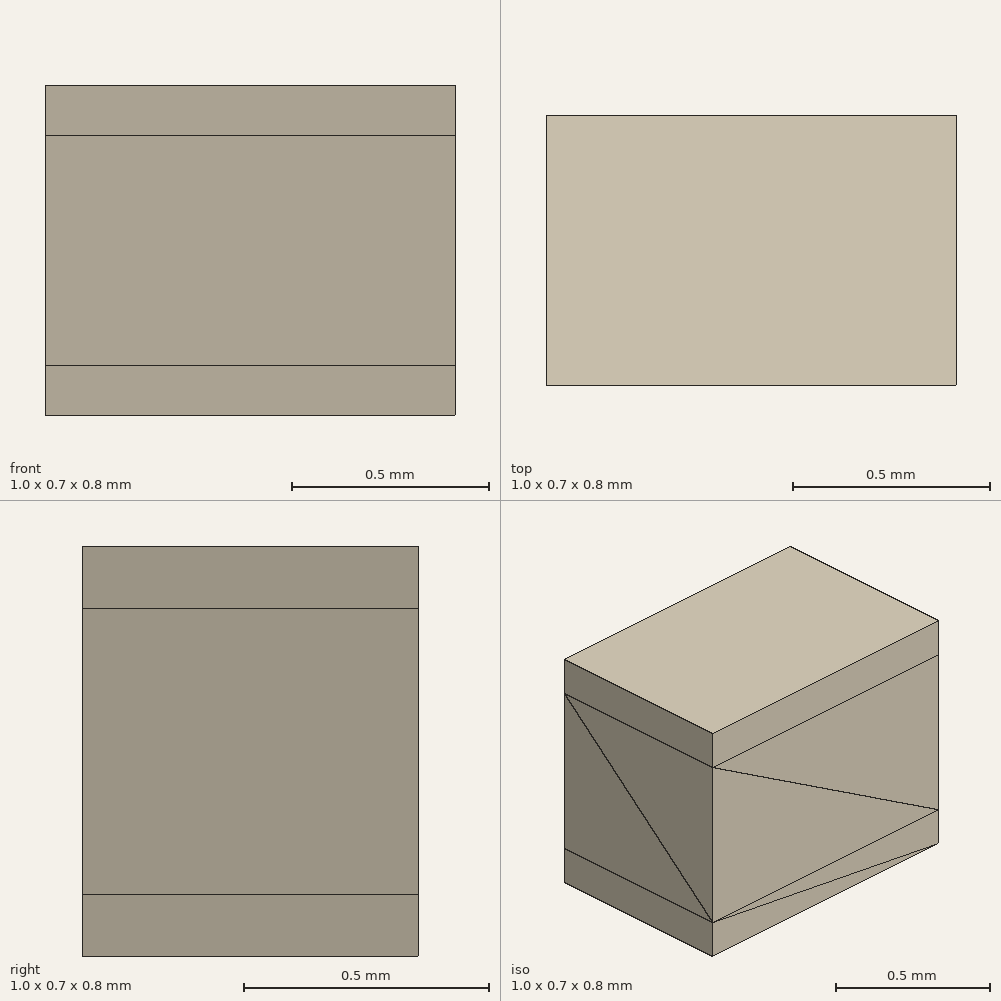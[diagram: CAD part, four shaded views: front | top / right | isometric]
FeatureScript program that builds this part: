
annotation { "Feature Type Name" : "Feature", "Feature Type Description" : "" }
export const myFeature = defineFeature(function(context is Context, id is Id, definition is map)
    precondition{}
    {
        {
            var Q0;
            Q0=qCreatedBy(makeId("Top.planeOp"),FACE);
            var sketch = newSketch(context, id + "F0", { "sketchPlane" : qUnion([Q0])});
            skLineSegment(sketch, "E0.bottom", {"start": v(-0.52, 0.34) * mm, "end": v(0.52, 0.34) * mm});
            skLineSegment(sketch, "E0.top", {"start": v(-0.52, -0.34) * mm, "end": v(0.52, -0.34) * mm});
            skLineSegment(sketch, "E0.left", {"start": v(-0.52, 0.34) * mm, "end": v(-0.52, -0.34) * mm});
            skLineSegment(sketch, "E0.right", {"start": v(0.52, 0.34) * mm, "end": v(0.52, -0.34) * mm});
            skSolve(sketch);
        }
        {
            var Q0;
            Q0 = qSketchRegion(id + "F0", true);
            extrude(context, id + "F1", {"entities" : qUnion([Q0]), "depth" : 0.13 * mm});
        }
        {
            var Q0;
            Q0 = qSketchRegion(id + "F0", true);
            extrude(context, id + "F2", {"entities" : qUnion([Q0]), "oppositeDirection" : true, "depth" : 0.58 * mm});
        }
        {
            var Q0;
            Q0=makeQuery(id+"F2.opExtrude","CAP_FACE",FACE,{"disambiguationData":[OSD([sQuery(id+"F0.wireOp",EDGE,"E0.bottom"),sQuery(id+"F0.wireOp",EDGE,"E0.top"),sQuery(id+"F0.wireOp",EDGE,"E0.left"),sQuery(id+"F0.wireOp",EDGE,"E0.right")])],"isStart":false});
            var sketch = newSketch(context, id + "F3", { "sketchPlane" : qUnion([Q0])});
            skLineSegment(sketch, "E1.bottom", {"start": v(0.52, 0.34) * mm, "end": v(-0.52, 0.34) * mm});
            skLineSegment(sketch, "E1.top", {"start": v(0.52, -0.34) * mm, "end": v(-0.52, -0.34) * mm});
            skLineSegment(sketch, "E1.left", {"start": v(0.52, 0.34) * mm, "end": v(0.52, -0.34) * mm});
            skLineSegment(sketch, "E1.right", {"start": v(-0.52, 0.34) * mm, "end": v(-0.52, -0.34) * mm});
            skSolve(sketch);
        }
        {
            var Q0;
            Q0 = qSketchRegion(id + "F3", true);
            extrude(context, id + "F4", {"entities" : qUnion([Q0]), "depth" : 0.13 * mm});
        }
    });
